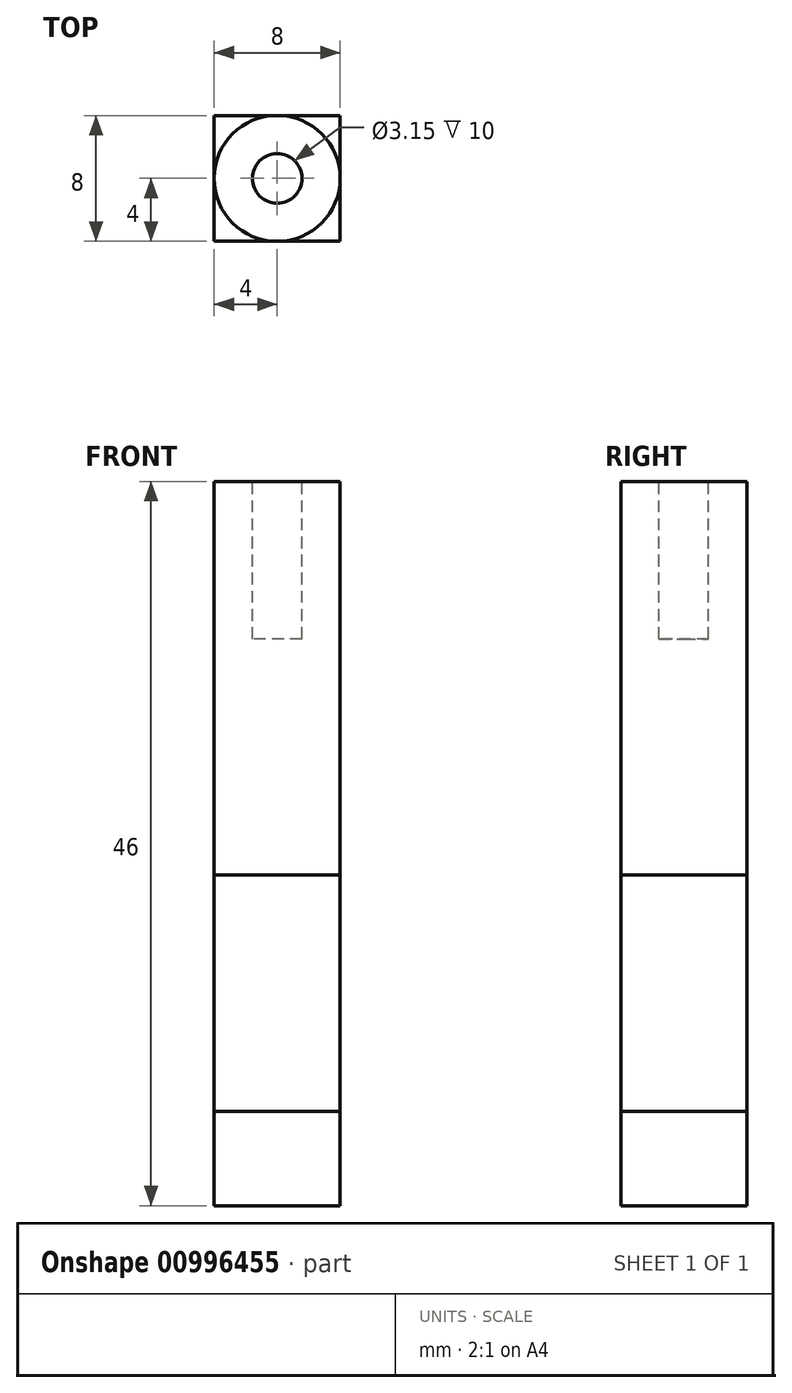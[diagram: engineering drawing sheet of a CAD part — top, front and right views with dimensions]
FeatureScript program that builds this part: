
annotation { "Feature Type Name" : "Feature", "Feature Type Description" : "" }
export const myFeature = defineFeature(function(context is Context, id is Id, definition is map)
    precondition{}
    {
        {
            var Q0;
            Q0=qCreatedBy(makeId("Top.planeOp"),FACE);
            var sketch = newSketch(context, id + "F0", { "sketchPlane" : qUnion([Q0])});
            skCircle(sketch, "E0", {"center": v(0, 0) * mm, "radius": 4 * mm});
            skSolve(sketch);
        }
        {
            var Q0;
            Q0=qSketchRegion(id+"F0",true);
            extrude(context, id + "F1", {"entities" : qUnion([Q0]), "depth" : 6 * mm, "offsetDistance" : 25 * mm});
        }
        {
            var Q0;
            Q0=makeQuery(id+"F1.opExtrude","CAP_FACE",FACE,{"disambiguationData":[OSD([sQuery(id+"F0.wireOp",EDGE,"E0")])],"isStart":false});
            var sketch = newSketch(context, id + "F2", { "sketchPlane" : qUnion([Q0])});
            skLineSegment(sketch, "E1.bottom", {"start": v(4, 4) * mm, "end": v(-4, 4) * mm});
            skLineSegment(sketch, "E1.top", {"start": v(4, -4) * mm, "end": v(-4, -4) * mm});
            skLineSegment(sketch, "E1.left", {"start": v(4, 4) * mm, "end": v(4, -4) * mm});
            skLineSegment(sketch, "E1.right", {"start": v(-4, 4) * mm, "end": v(-4, -4) * mm});
            skPoint(sketch, "E1.middle", {"position": v(0, 0) * mm});
            skSolve(sketch);
        }
        {
            var Q0;
            Q0=qSketchRegion(id+"F2",true);
            extrude(context, id + "F3", {"entities" : qUnion([Q0]), "operationType" : NewBodyOperationType.ADD, "depth" : 15 * mm, "offsetDistance" : 25 * mm});
        }
        {
            var Q0;
            Q0=makeQuery(id+"F3.opExtrude","CAP_FACE",FACE,{"disambiguationData":[OSD([sQuery(id+"F2.wireOp",EDGE,"E1.bottom"),sQuery(id+"F2.wireOp",EDGE,"E1.top"),sQuery(id+"F2.wireOp",EDGE,"E1.left"),sQuery(id+"F2.wireOp",EDGE,"E1.right")])],"isStart":false});
            var sketch = newSketch(context, id + "F4", { "sketchPlane" : qUnion([Q0])});
            skCircle(sketch, "E2", {"center": v(0, 0) * mm, "radius": 4 * mm});
            skSolve(sketch);
        }
        {
            var Q0;
            Q0=qSketchRegion(id+"F4",true);
            extrude(context, id + "F5", {"entities" : qUnion([Q0]), "operationType" : NewBodyOperationType.ADD, "depth" : 25 * mm, "offsetDistance" : 25 * mm});
        }
        {
            var Q0;
            Q0=makeQuery(id+"F5.opExtrude","CAP_FACE",FACE,{"disambiguationData":[OSD([sQuery(id+"F4.wireOp",EDGE,"E2")])],"isStart":false});
            var sketch = newSketch(context, id + "F6", { "sketchPlane" : qUnion([Q0])});
            skCircle(sketch, "E3", {"center": v(0, 0) * mm, "radius": 1.57 * mm});
            skSolve(sketch);
        }
        {
            var Q0;
            Q0=qSketchRegion(id+"F6",true);
            extrude(context, id + "F7", {"entities" : qUnion([Q0]), "operationType" : NewBodyOperationType.REMOVE, "oppositeDirection" : true, "depth" : 10 * mm, "offsetDistance" : 25 * mm});
        }
    });
